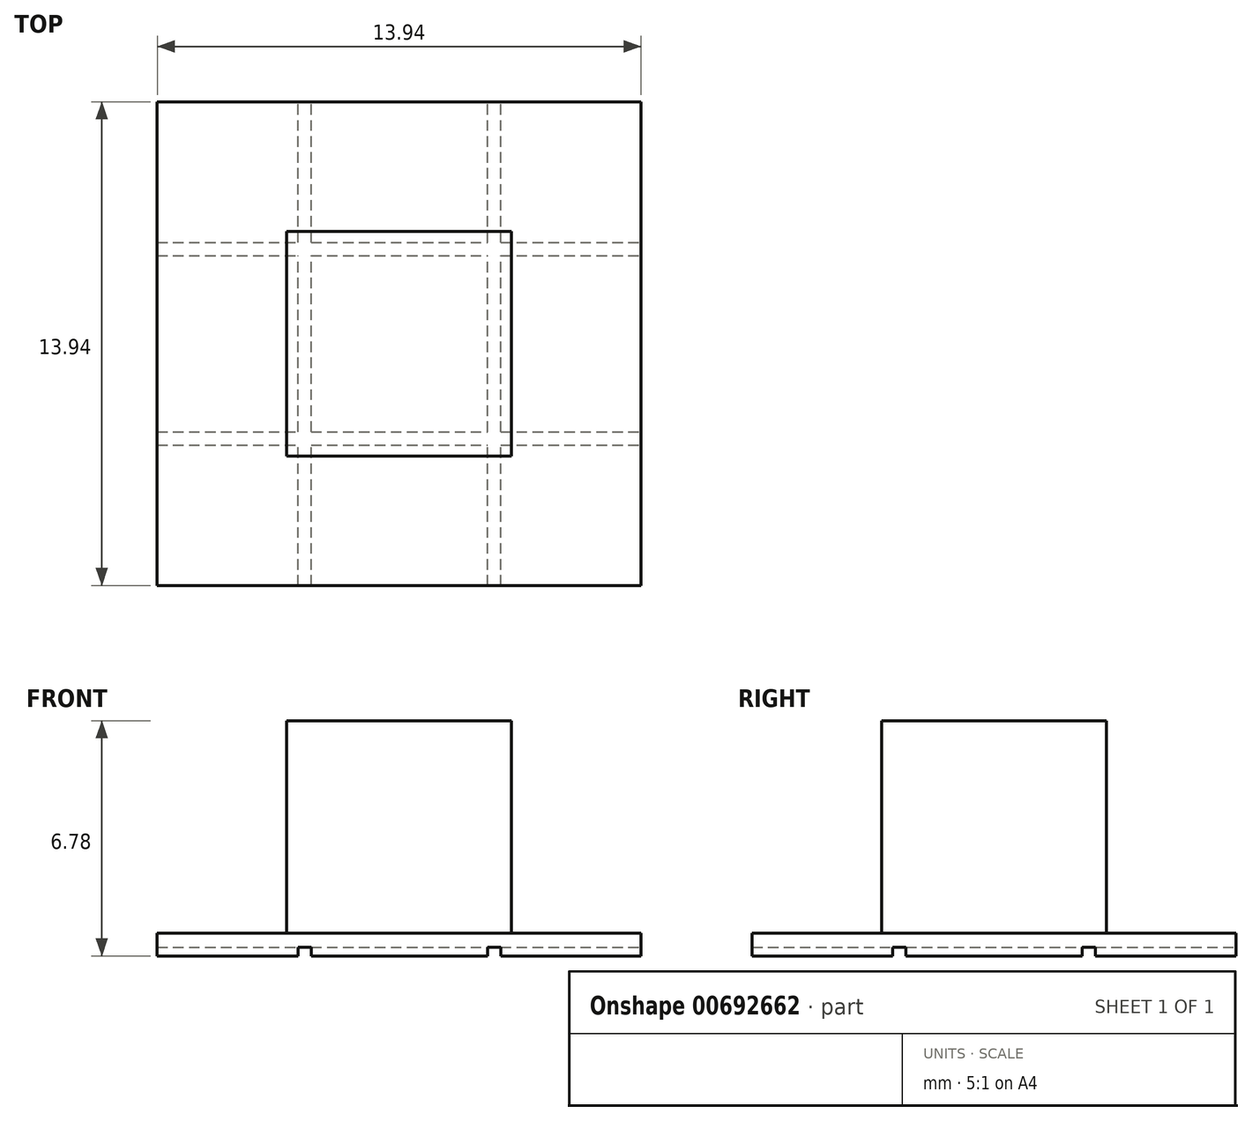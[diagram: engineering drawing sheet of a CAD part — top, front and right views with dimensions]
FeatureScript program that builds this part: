
annotation { "Feature Type Name" : "Feature", "Feature Type Description" : "" }
export const myFeature = defineFeature(function(context is Context, id is Id, definition is map)
    precondition{}
    {
        {
            var Q0;
            Q0=qCreatedBy(makeId("Top.planeOp"),FACE);
            var sketch = newSketch(context, id + "F0", { "sketchPlane" : qUnion([Q0])});
            skLineSegment(sketch, "E0.bottom", {"start": v(-13.08, 14.86) * mm, "end": v(-6.6, 14.86) * mm});
            skLineSegment(sketch, "E0.top", {"start": v(-13.08, 8.38) * mm, "end": v(-6.6, 8.38) * mm});
            skLineSegment(sketch, "E0.left", {"start": v(-13.08, 14.86) * mm, "end": v(-13.08, 8.38) * mm});
            skLineSegment(sketch, "E0.right", {"start": v(-6.6, 14.86) * mm, "end": v(-6.6, 8.38) * mm});
            skSolve(sketch);
        }
        {
            var Q0;
            Q0=makeQuery(id+"F0.imprint","IMPRINT",FACE,{"disambiguationData":[TD([[makeQuery(id+"F0.imprint","IMPRINT",EDGE,{"derivedFrom":sQuery(id+"F0.wireOp",EDGE,"E0.bottom")}),-1.0]])]});
            extrude(context, id + "F1", {"entities" : qUnion([Q0]), "depth" : 6.48 * mm, "offsetDistance" : 25.4 * mm});
        }
        {
            var Q0;
            Q0=makeQuery(id+"F1.opExtrude","SWEPT_BODY",BODY,{"disambiguationData":[OSD([sQuery(id+"F0.wireOp",EDGE,"E0.bottom"),sQuery(id+"F0.wireOp",EDGE,"E0.top"),sQuery(id+"F0.wireOp",EDGE,"E0.left"),sQuery(id+"F0.wireOp",EDGE,"E0.right")])]});
            transform(context, id + "F2", {"entities" : qUnion([Q0]), "transformType" : TransformType.TRANSLATION_3D, "dx" : 9.85 * mm, "dy" : -11.62 * mm, "dz" : 0 * mm, "makeCopy" : false});
        }
        {
            var Q0;
            Q0=qCreatedBy(makeId("Top.planeOp"),FACE);
            var sketch = newSketch(context, id + "F3", { "sketchPlane" : qUnion([Q0])});
            skLineSegment(sketch, "E1.0", {"start": v(-6.97, 6.97) * mm, "end": v(-6.97, -6.97) * mm});
            skLineSegment(sketch, "E1.1", {"start": v(6.98, 6.97) * mm, "end": v(-6.97, 6.97) * mm});
            skLineSegment(sketch, "E1.2", {"start": v(6.98, -6.97) * mm, "end": v(6.98, 6.97) * mm});
            skLineSegment(sketch, "E1.3", {"start": v(-6.97, -6.97) * mm, "end": v(6.98, -6.97) * mm});
            skSolve(sketch);
        }
        {
            var Q0;
            Q0=makeQuery(id+"F3.imprint","IMPRINT",FACE,{"disambiguationData":[TD([[makeQuery(id+"F3.imprint","IMPRINT",EDGE,{"derivedFrom":sQuery(id+"F3.wireOp",EDGE,"E1.0")}),1.0]])]});
            extrude(context, id + "F4", {"entities" : qUnion([Q0]), "operationType" : NewBodyOperationType.ADD, "depth" : 6.78 * mm, "offsetDistance" : 25.4 * mm, "hasSecondDirection" : true, "secondDirectionOppositeDirection" : false, "secondDirectionDepth" : 6.12 * mm});
        }
        {
            var Q0;
            Q0=qCreatedBy(makeId("Front.planeOp"),FACE);
            var sketch = newSketch(context, id + "F5", { "sketchPlane" : qUnion([Q0])});
            skLineSegment(sketch, "E2.bottom", {"start": v(-2.92, 7.4) * mm, "end": v(-2.54, 7.4) * mm});
            skLineSegment(sketch, "E2.top", {"start": v(-2.92, 6.53) * mm, "end": v(-2.54, 6.53) * mm});
            skLineSegment(sketch, "E2.left", {"start": v(-2.92, 7.4) * mm, "end": v(-2.92, 6.53) * mm});
            skLineSegment(sketch, "E2.right", {"start": v(-2.54, 7.4) * mm, "end": v(-2.54, 6.53) * mm});
            skLineSegment(sketch, "E3.MirrorCS", {"start": v(2.92, 7.4) * mm, "end": v(2.54, 7.4) * mm});
            skLineSegment(sketch, "E4.MirrorCS", {"start": v(2.92, 7.4) * mm, "end": v(2.92, 6.53) * mm});
            skLineSegment(sketch, "E5.MirrorCS", {"start": v(2.54, 7.4) * mm, "end": v(2.54, 6.53) * mm});
            skLineSegment(sketch, "E6.MirrorCS", {"start": v(2.92, 6.53) * mm, "end": v(2.54, 6.53) * mm});
            skSolve(sketch);
        }
        {
            var Q0;
            Q0=makeQuery(id+"F5.imprint","IMPRINT",FACE,{"disambiguationData":[TD([[makeQuery(id+"F5.imprint","IMPRINT",EDGE,{"derivedFrom":sQuery(id+"F5.wireOp",EDGE,"E2.bottom")}),-1.0]])]});
            var Q1;
            Q1=makeQuery(id+"F5.imprint","IMPRINT",FACE,{"disambiguationData":[TD([[makeQuery(id+"F5.imprint","IMPRINT",EDGE,{"derivedFrom":sQuery(id+"F5.wireOp",EDGE,"E3.MirrorCS")}),1.0]])]});
            extrude(context, id + "F6", {"entities" : qUnion([Q0, Q1]), "operationType" : NewBodyOperationType.REMOVE, "endBound" : BoundingType.SYMMETRIC, "depth" : 25.4 * mm, "offsetDistance" : 25.4 * mm, "hasSecondDirection" : true, "secondDirectionOppositeDirection" : true, "secondDirectionDepth" : 25.4 * mm});
        }
        {
            var Q0;
            Q0=qCreatedBy(makeId("Right.planeOp"),FACE);
            var sketch = newSketch(context, id + "F7", { "sketchPlane" : qUnion([Q0])});
            skLineSegment(sketch, "E7.bottom", {"start": v(-2.92, 7.88) * mm, "end": v(-2.54, 7.88) * mm});
            skLineSegment(sketch, "E7.top", {"start": v(-2.92, 6.53) * mm, "end": v(-2.54, 6.53) * mm});
            skLineSegment(sketch, "E7.left", {"start": v(-2.92, 7.88) * mm, "end": v(-2.92, 6.53) * mm});
            skLineSegment(sketch, "E7.right", {"start": v(-2.54, 7.88) * mm, "end": v(-2.54, 6.53) * mm});
            skLineSegment(sketch, "E8.MirrorCS", {"start": v(2.92, 7.88) * mm, "end": v(2.54, 7.88) * mm});
            skLineSegment(sketch, "E9.MirrorCS", {"start": v(2.92, 7.88) * mm, "end": v(2.92, 6.53) * mm});
            skLineSegment(sketch, "E10.MirrorCS", {"start": v(2.54, 7.88) * mm, "end": v(2.54, 6.53) * mm});
            skLineSegment(sketch, "E11.MirrorCS", {"start": v(2.92, 6.53) * mm, "end": v(2.54, 6.53) * mm});
            skSolve(sketch);
        }
        {
            var Q0;
            Q0=makeQuery(id+"F7.imprint","IMPRINT",FACE,{"disambiguationData":[TD([[makeQuery(id+"F7.imprint","IMPRINT",EDGE,{"derivedFrom":sQuery(id+"F7.wireOp",EDGE,"E7.bottom")}),-1.0]])]});
            var Q1;
            Q1=makeQuery(id+"F7.imprint","IMPRINT",FACE,{"disambiguationData":[TD([[makeQuery(id+"F7.imprint","IMPRINT",EDGE,{"derivedFrom":sQuery(id+"F7.wireOp",EDGE,"E8.MirrorCS")}),1.0]])]});
            extrude(context, id + "F8", {"entities" : qUnion([Q0, Q1]), "operationType" : NewBodyOperationType.REMOVE, "endBound" : BoundingType.SYMMETRIC, "depth" : 25.4 * mm, "offsetDistance" : 25.4 * mm, "hasSecondDirection" : true, "secondDirectionOppositeDirection" : true, "secondDirectionDepth" : 25.4 * mm});
        }
        {
            var Q0;
            Q0=makeQuery(id+"F1.opExtrude","SWEPT_BODY",BODY,{"disambiguationData":[OSD([sQuery(id+"F0.wireOp",EDGE,"E0.bottom"),sQuery(id+"F0.wireOp",EDGE,"E0.top"),sQuery(id+"F0.wireOp",EDGE,"E0.left"),sQuery(id+"F0.wireOp",EDGE,"E0.right")])]});
            var Q1;
            Q1=makeQuery(id+"F1.opExtrude","CAP_EDGE",EDGE,{"disambiguationData":[OSD([sQuery(id+"F0.wireOp",EDGE,"E0.left")])],"isStart":true});
            transform(context, id + "F9", {"entities" : qUnion([Q0]), "transformType" : TransformType.ROTATION, "transformAxis" : qUnion([Q1]), "angle" : 180 * degree, "makeCopy" : false});
        }
    });
